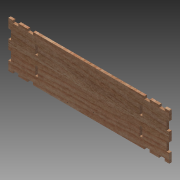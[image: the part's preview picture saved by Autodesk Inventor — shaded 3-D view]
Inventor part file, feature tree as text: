
AUTODESK INVENTOR PART (.ipt)
format: ipt  version: 2014 SP1 (Build 180222100, 222)  size: 381,952 bytes
history: native  units: mm
features: other x9, sketch x5, extrude x3
ambient origin geometry x8: Origin, YZ Plane, XZ Plane, XY Plane, X Axis, Y Axis, Z Axis, Center Point
bodies: Solid1 (feature_tree)
feature tree (17):
  other  "Blocks"
  extrude  "Extrusion1"  Depth=100.0mm
  extrude  "Extrusion2"  Depth=20.0mm
  extrude  "Extrusion5"  Depth=20.0mm
  sketch  "Sketch18"  dims[d34=20.0mm]
  sketch  "Sketch19"  dims[d35=20.0mm d36=20.0mm d37=20.0mm d38=20.0mm d39=5.5mm d40=5.5mm d41=5.5mm d42=5.5mm d43=53.0mm d44=53.0mm d45=10.0mm d46=0.0mm d54=12.0mm d55=20.0mm d58=5.5mm d59=10.0mm d60=0.0mm d61=64.0mm]
  sketch  "Sketch17"  dims[d32=20.0mm d33=20.0mm]
  sketch  "Sketch6"  dims[d0=350.0mm d1=100.0mm]
  sketch  "Sketch8"  dims[d2=5.5mm d3=0.0mm d31=20.0mm]
  other  "Block1"
  other  "Block2"
  other  "Block3"
  other  "Block4"
  other  "Block3:1"
  other  "Block3:2"
  other  "Block4:1"
  other  "Block4:2"
